# Revit family: Camera-Security-Panasonic-Super_Dynamic-Weatherproof-Network-S1531LNSeriesX
name_source: partatom
category: Security Devices
revit_build: Autodesk Revit 2016 (Build: 20150714_1515(x64)
units: mm (PartAtom-declared; Revit-internal decimal feet)

## family parameters
Cut with Voids When Loaded = No
Host = Face
Maintain Annotation Orientation = No
OmniClass Number = 23.85.10.14.11
OmniClass Title = Cameras
Part Type = Normal
Room Calculation Point = No
Round Connector Dimension = Use Diameter
Shared = No

## types (3) — shared parameters
Alarm Input Or Output Specification = ALARM IN 1 (DAY/NIGHT IN), ALARM IN 2 (ALARM OUT), ALARM IN 3 (AUX OUT)
Audio In = Yes
Audio Out = Yes
Communication Ports = 10Base-T / 100Base-TX, RJ45 connector
Day Or Night = Yes
Equipment Abbreviation = SC
Family Version = 1.0.0
Has POE = Yes
IP Or Analog = IP
Indoor Or Outdoor = Outdoor
Manufacturer = Panasonic
Model Disclaimer = Contact Panasonic for more information
Mounting Positions = Mount Dependent or Surface Mount
Operational Temperature = -40 °F to 140 °F
Panning Range = -100 to +100
Product Documentation Link = http://ssbu-t.psn-web.net
Product Material = Paint - Panasonic - Light Gray
Product Page URL = http://security.panasonic.com
Provide Feedback = https://www.surveymonkey.com
Regulatory Compliance = UL UL60950-1, C-UL CAN/CSA C22.2 No.60950-1, CE, IEC60950-1 FCC Part15 ClassA, ICES003 ClassA, EN55022 ClassB, EN55024
Shock Resistance = Compliant with IK10 (IEC 62262)
Storage Temperature = -40 °F to 140 °F
Super Dynamic Range = Yes
Tilting Range = -100 to +100
URL = http://security.panasonic.com
Vandal Resistant = Yes
Voltage DC = 12 V
Water and Dust Resistance = IP66, IEC60529 measuring standard compatible, Type 4X(UL50), NEMA 4X compliant
Width = 3.74 "
Yaw Max = 100.00°
Yaw Min = -190.00°
Yawing Range = -190 to +100
z Base Square = Yes
z Camera Center Offset = 0.287 "
z Camera Center Offset Base = 1.181 "
z Column Height = 3.11 "
z Const CameraYawAxis = 15.748 "
z Const Pan Handle Length = 27.559 "
z Const Tilt Base Length = 9.843 "
z Const Tilt Base2 Length = 19.685 "
z Const Tilt Handle Length = 14.173 "
z Const Yaw Axis Length = 7.874 "
z Const Yaw Base Length = 10.236 "
z Const Yaw Base2 Length = 17.323 "
z Const Yaw Handle Length = 9.252 "
z Hinge Height = 3.799 "
zero-valued in all types: Default Elevation

## per-type parameters (varying)
| type | Angle Of View | Date Last Modified | Description | HFOV Max 169 | HFOV Max 43 | HFOV Min 169 | HFOV Min 43 | Minimum Illumination | Model | Operational Humidity | Part Description | Part Number | Power Active | VFOV Max 169 | VFOV Max 43 | VFOV Min 169 | VFOV Min 43 | z Camera Type | z VV Viewpoint Depth Max | z VV Viewpoint Depth Min |
| Full HD, WV-S1531LN | 112 | December, 15, 2016 | Security Camera, Super Dynamic, Full HD, Weatherproof, Network, WV-S1531LN | 112.00° | 91.00° | 31.00° | 26.00° | 0.012 lx | WV-S1531LN | 10% to 90% (no condensation) | Security Camera, Super Dynamic, Full HD, Weatherproof, Network, WV-S1531LN | WV-S1531LN | 9.6 W | 60.00° | 67.00° | 17.00° | 19.00° | No | 8.134 " | 7.81 " |
| HD, WV-S1511LN | 112 | December, 15, 2016 | Security Camera, Super Dynamic, HD, Weatherproof, Network, WV-S1511LN | 112.00° | 91.00° | 31.00° | 26.00° | 0.008 lx | WV-S1511LN | 10% to 90% (no condensation) | Security Camera, Super Dynamic, HD, Weatherproof, Network, WV-S1511LN | WV-S1511LN | 9.0 W | 60.00° | 67.00° | 17.00° | 19.00° | No | 8.134 " | 7.81 " |
| Full HD, WV-S1531LTN | 34 | June, 1, 2017 | Security Camera, Super Dynamic, Full HD, Weatherproof, Network, WV-S1531LTN | 34.00° | 28.00° | 14.00° | 12.00° | 0.015 lx | WV-S1531LTN | 10 to 100 % (no condensation) | Security Camera, Super Dynamic, Full HD, Weatherproof, Network, WV-S1531LTN | WV-S1531LTN | 9.0 W | 19.00° | 21.00° | 8.00° | 9.00° | Yes | 8.128 " | 7.796 " |

## geometry (parser evidence)
native form markers: Sweep x8
no freeform markers — native parametric forms only
